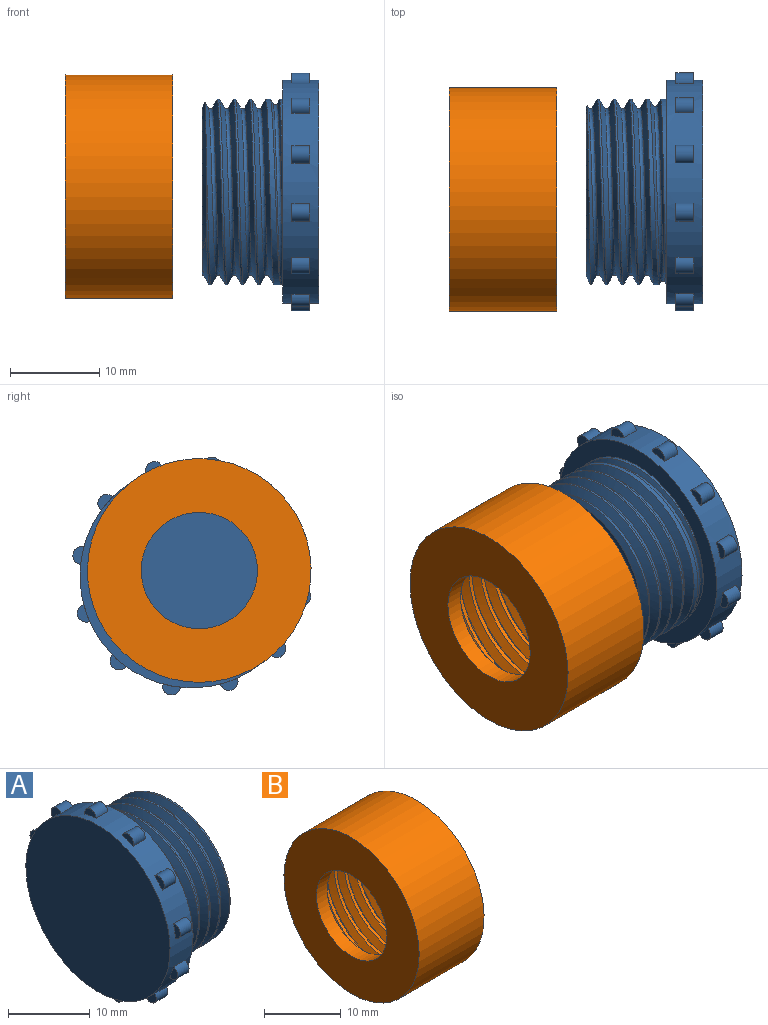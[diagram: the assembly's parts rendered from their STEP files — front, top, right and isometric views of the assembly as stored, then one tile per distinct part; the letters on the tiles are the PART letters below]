
ASSEMBLY  parts=2 mates=1
PART A: 49 faces, bbox 14x26.7x26.7 mm
  f0: cylinder r=10.38mm len=20.75mm, axis (-1,0,0), area 105.7mm2, adj f35,f41,f42,f43,f46,f47,f48
  f1: plane 1.99x1.22mm, normal (1,0,0), area 1.6mm2, adj f2,f34
  f2: cylinder r=1mm len=2mm, axis (-1,0,0), area 6.4mm2, adj f1,f3,f34
  f3: plane 1.99x1.22mm, normal (-1,0,0), area 1.6mm2, adj f2,f34
  f4: plane 1.79x1.68mm, normal (1,0,0), area 1.6mm2, adj f5,f34
  f5: cylinder r=1mm len=2mm, axis (-1,0,0), area 6.4mm2, adj f4,f6,f34
  f6: plane 1.79x1.68mm, normal (-1,0,0), area 1.6mm2, adj f5,f34
  f7: plane 1.96x1.37mm, normal (1,0,0), area 1.6mm2, adj f8,f34
  f8: cylinder r=1mm len=2mm, axis (-1,0,0), area 6.4mm2, adj f7,f9,f34
  f9: plane 1.96x1.37mm, normal (-1,0,0), area 1.6mm2, adj f8,f34
  f10: plane 1.99x1.22mm, normal (1,0,0), area 1.6mm2, adj f11,f34
  f11: cylinder r=1mm len=2mm, axis (-1,0,0), area 6.4mm2, adj f10,f12,f34
  f12: plane 1.99x1.22mm, normal (-1,0,0), area 1.6mm2, adj f11,f34
  f13: plane 1.79x1.68mm, normal (1,0,0), area 1.6mm2, adj f14,f34
  f14: cylinder r=1mm len=2mm, axis (-1,0,0), area 6.4mm2, adj f13,f15,f34
  f15: plane 1.79x1.68mm, normal (-1,0,0), area 1.6mm2, adj f14,f34
  f16: plane 1.96x1.37mm, normal (1,0,0), area 1.6mm2, adj f17,f34
  f17: cylinder r=1mm len=2mm, axis (-1,0,0), area 6.4mm2, adj f16,f18,f34
  f18: plane 1.96x1.37mm, normal (-1,0,0), area 1.6mm2, adj f17,f34
  f19: plane 1.99x1.22mm, normal (1,0,0), area 1.6mm2, adj f20,f34
  f20: cylinder r=1mm len=2mm, axis (-1,0,0), area 6.4mm2, adj f19,f21,f34
  f21: plane 1.99x1.22mm, normal (-1,0,0), area 1.6mm2, adj f20,f34
  f22: plane 1.79x1.68mm, normal (1,0,0), area 1.6mm2, adj f23,f34
  f23: cylinder r=1mm len=2mm, axis (-1,0,0), area 6.4mm2, adj f22,f24,f34
  f24: plane 1.79x1.68mm, normal (-1,0,0), area 1.6mm2, adj f23,f34
  f25: plane 1.96x1.37mm, normal (1,0,0), area 1.6mm2, adj f26,f34
  f26: cylinder r=1mm len=2mm, axis (-1,0,0), area 6.4mm2, adj f25,f27,f34
  f27: plane 1.96x1.37mm, normal (-1,0,0), area 1.6mm2, adj f26,f34
  f28: plane 1.99x1.22mm, normal (1,0,0), area 1.6mm2, adj f29,f34
  f29: cylinder r=1mm len=2mm, axis (-1,0,0), area 6.4mm2, adj f28,f30,f34
  f30: plane 1.99x1.22mm, normal (-1,0,0), area 1.6mm2, adj f29,f34
  f31: plane 1.79x1.68mm, normal (1,0,0), area 1.6mm2, adj f32,f34
  f32: cylinder r=1mm len=2mm, axis (-1,0,0), area 6.4mm2, adj f31,f33,f34
  f33: plane 1.79x1.68mm, normal (-1,0,0), area 1.6mm2, adj f32,f34
  f34: cylinder r=12.5mm len=25mm, axis (-1,0,0), area 266.1mm2, adj f1,f2,f3,f4,f5,f6,f7,f8
  f35: plane 25.04x25.04mm, normal (1,0,0), area 155.1mm2, adj f0,f34,f41,f42,f44
  f36: plane 25x25mm, normal (-1,0,0), area 490.9mm2, adj f34
  f37: plane 19.07x18.9mm, normal (1,0,0), area 279.5mm2, adj f45,f46,f47,f48
  f38: plane 1.96x1.37mm, normal (1,0,0), area 1.6mm2, adj f34,f39
  f39: cylinder r=1mm len=2mm, axis (-1,0,0), area 6.4mm2, adj f34,f38,f40
  f40: plane 1.96x1.37mm, normal (-1,0,0), area 1.6mm2, adj f34,f39
  f41: plane 0.26x0.18mm, normal (0,-1,0), area 0mm2, adj f0,f35,f43,f44
  f42: bspline ~21.82x21.29mm, area 36.4mm2, adj f0,f35,f44,f47
  f43: bspline ~22.09x21.64mm, area 38.4mm2, adj f0,f41,f44,f46
  f44: bspline ~20.22x19.84mm, area 30mm2, adj f35,f41,f42,f43,f45
  f45: bspline ~21.7x18.79mm, area 118.4mm2, adj f37,f44,f46,f47
  f46: bspline ~23.96x20.75mm, area 251.6mm2, adj f0,f37,f43,f45,f48
  f47: bspline ~23.96x20.75mm, area 291.8mm2, adj f0,f37,f42,f45,f48
  f48: cone r=10.38mm half-angle=63.4deg, axis (-1,0,0), area 25.8mm2, adj f0,f37,f46,f47
PART B: 12 faces, bbox 13.4x25.6x25.6 mm
  f0: plane 20.34x20.14mm, normal (1,0,0), area 178.9mm2, adj f1,f7,f8,f9,f11
  f1: cylinder r=6.5mm len=13mm, axis (-1,0,0), area 81.7mm2, adj f0,f2
  f2: plane 25x25mm, normal (-1,0,0), area 358.1mm2, adj f1,f3
  f3: cylinder r=12.5mm len=25mm, axis (-1,0,0), area 942.5mm2, adj f2,f4
  f4: plane 25.58x25.58mm, normal (1,0,0), area 166.6mm2, adj f3,f5,f6,f10,f11
  f5: bspline ~24.71x21.4mm, area 389.7mm2, adj f4,f8,f10,f11
  f6: bspline ~24.71x21.4mm, area 358.4mm2, adj f4,f7,f10,f11
  f7: bspline ~21.03x19.21mm, area 28.2mm2, adj f0,f6,f9,f11
  f8: bspline ~16.8x10.56mm, area 11.4mm2, adj f0,f5,f9
  f9: bspline ~21.08x10.65mm, area 6.5mm2, adj f0,f7,f8,f10
  f10: bspline ~24.9x21.56mm, area 91.1mm2, adj f4,f5,f6,f9
  f11: cylinder r=9.72mm len=19.44mm, axis (1,0,0), area 163.1mm2, adj f0,f4,f5,f6,f7
PLACE A rot(axis=(0,1,0),180deg) t=(7.23,-118.39,109.49)mm
PLACE B t=(-21.1,-70.34,4.11)mm
MATE cylindrical A.f0 <-> B.f4  axis (-1,0,0) through (3.23,24.17,52.09)mm
